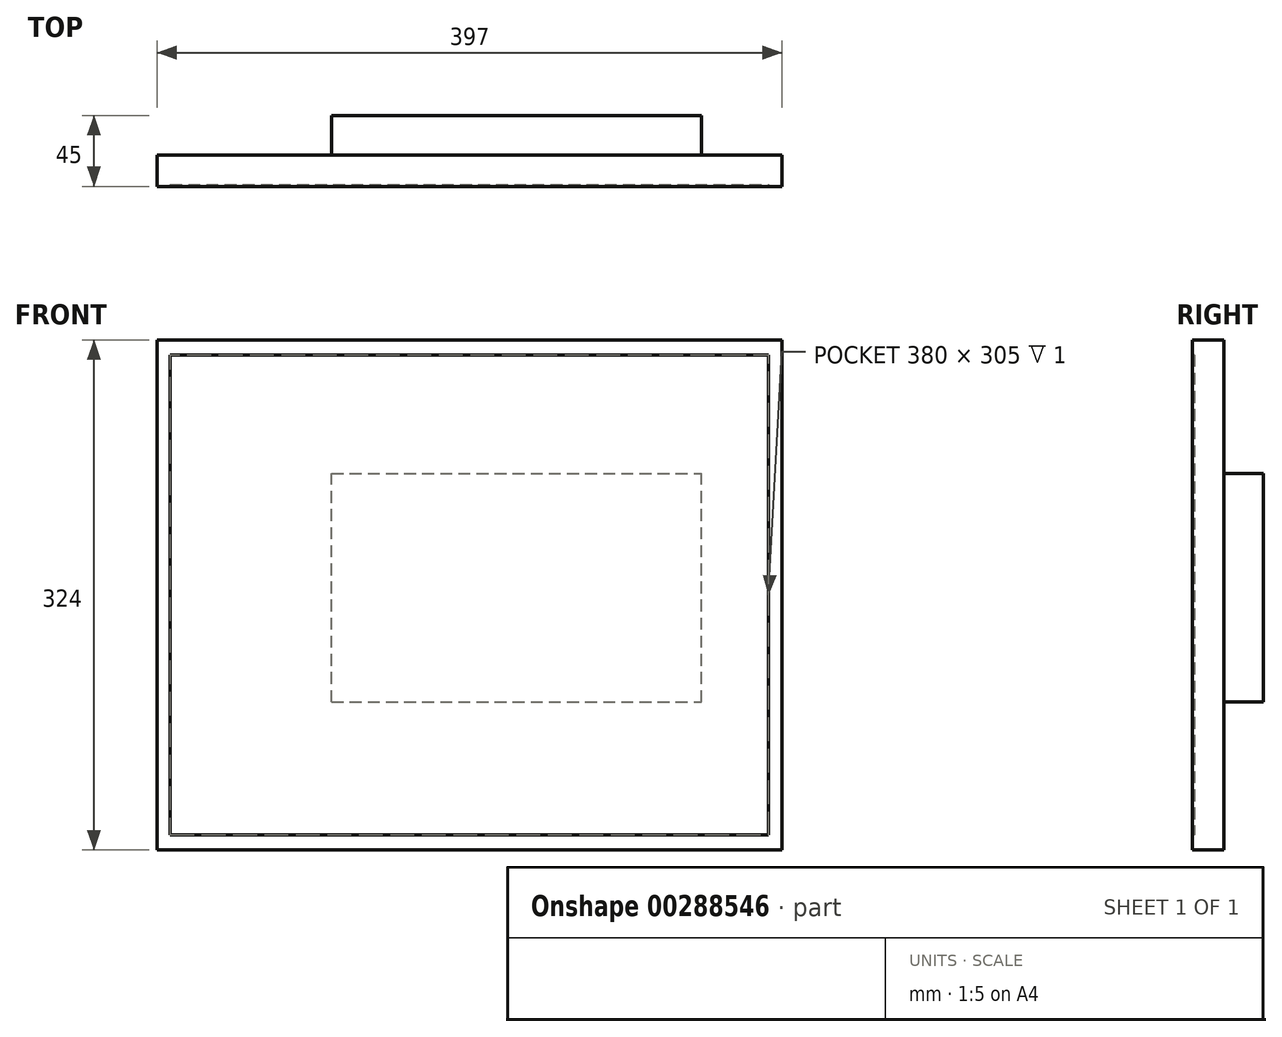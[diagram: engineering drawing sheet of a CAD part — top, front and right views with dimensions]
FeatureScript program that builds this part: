
annotation { "Feature Type Name" : "Feature", "Feature Type Description" : "" }
export const myFeature = defineFeature(function(context is Context, id is Id, definition is map)
    precondition{}
    {
        {
            var Q0;
            Q0=qCreatedBy(makeId("Front.planeOp"),FACE);
            var sketch = newSketch(context, id + "F0", { "sketchPlane" : qUnion([Q0])});
            skLineSegment(sketch, "E0.bottom", {"start": v(-198.5, 162) * mm, "end": v(198.5, 162) * mm});
            skLineSegment(sketch, "E0.top", {"start": v(-198.5, -162) * mm, "end": v(198.5, -162) * mm});
            skLineSegment(sketch, "E0.left", {"start": v(-198.5, 162) * mm, "end": v(-198.5, -162) * mm});
            skLineSegment(sketch, "E0.right", {"start": v(198.5, 162) * mm, "end": v(198.5, -162) * mm});
            skPoint(sketch, "E0.middle", {"position": v(0, 0) * mm});
            skSolve(sketch);
        }
        {
            var Q0;
            Q0=makeQuery(id+"F0.imprint","IMPRINT",FACE,{"disambiguationData":[TD([[makeQuery(id+"F0.imprint","IMPRINT",EDGE,{"derivedFrom":sQuery(id+"F0.wireOp",EDGE,"E0.bottom")}),-1.0]])]});
            extrude(context, id + "F1", {"entities" : qUnion([Q0]), "depth" : 20 * mm});
        }
        {
            var Q0;
            Q0=makeQuery(id+"F1.opExtrude","CAP_FACE",FACE,{"disambiguationData":[OSD([sQuery(id+"F0.wireOp",EDGE,"E0.bottom"),sQuery(id+"F0.wireOp",EDGE,"E0.top"),sQuery(id+"F0.wireOp",EDGE,"E0.left"),sQuery(id+"F0.wireOp",EDGE,"E0.right")])],"isStart":false});
            var sketch = newSketch(context, id + "F2", { "sketchPlane" : qUnion([Q0])});
            skLineSegment(sketch, "E1.bottom", {"start": v(-190, 152.5) * mm, "end": v(190, 152.5) * mm});
            skLineSegment(sketch, "E1.top", {"start": v(-190, -152.5) * mm, "end": v(190, -152.5) * mm});
            skLineSegment(sketch, "E1.left", {"start": v(-190, 152.5) * mm, "end": v(-190, -152.5) * mm});
            skLineSegment(sketch, "E1.right", {"start": v(190, 152.5) * mm, "end": v(190, -152.5) * mm});
            skPoint(sketch, "E1.middle", {"position": v(0, 0) * mm});
            skSolve(sketch);
        }
        {
            var Q0;
            Q0=makeQuery(id+"F2.imprint","IMPRINT",FACE,{"disambiguationData":[TD([[makeQuery(id+"F2.imprint","IMPRINT",EDGE,{"derivedFrom":sQuery(id+"F2.wireOp",EDGE,"E1.bottom")}),-1.0]])]});
            extrude(context, id + "F3", {"entities" : qUnion([Q0]), "operationType" : NewBodyOperationType.REMOVE, "oppositeDirection" : true, "depth" : 1 * mm});
        }
        {
            var Q0;
            Q0=makeQuery(id+"F0.imprint","IMPRINT",FACE,{"disambiguationData":[TD([[makeQuery(id+"F0.imprint","IMPRINT",EDGE,{"derivedFrom":sQuery(id+"F0.wireOp",EDGE,"E0.bottom")}),-1.0]])]});
            var sketch = newSketch(context, id + "F4", { "sketchPlane" : qUnion([Q0])});
            skLineSegment(sketch, "E2.bottom", {"start": v(-87.5, -68) * mm, "end": v(147.5, -68) * mm});
            skLineSegment(sketch, "E2.top", {"start": v(-87.5, 77) * mm, "end": v(147.5, 77) * mm});
            skLineSegment(sketch, "E2.left", {"start": v(-87.5, -68) * mm, "end": v(-87.5, 77) * mm});
            skLineSegment(sketch, "E2.right", {"start": v(147.5, -68) * mm, "end": v(147.5, 77) * mm});
            skPoint(sketch, "E2.middle", {"position": v(30, 4.5) * mm});
            skSolve(sketch);
        }
        {
            var Q0;
            Q0=makeQuery(id+"F4.imprint","IMPRINT",FACE,{"disambiguationData":[TD([[makeQuery(id+"F4.imprint","IMPRINT",EDGE,{"derivedFrom":sQuery(id+"F4.wireOp",EDGE,"E2.bottom")}),1.0]])]});
            extrude(context, id + "F5", {"entities" : qUnion([Q0]), "operationType" : NewBodyOperationType.ADD, "oppositeDirection" : true, "depth" : 25 * mm});
        }
    });
